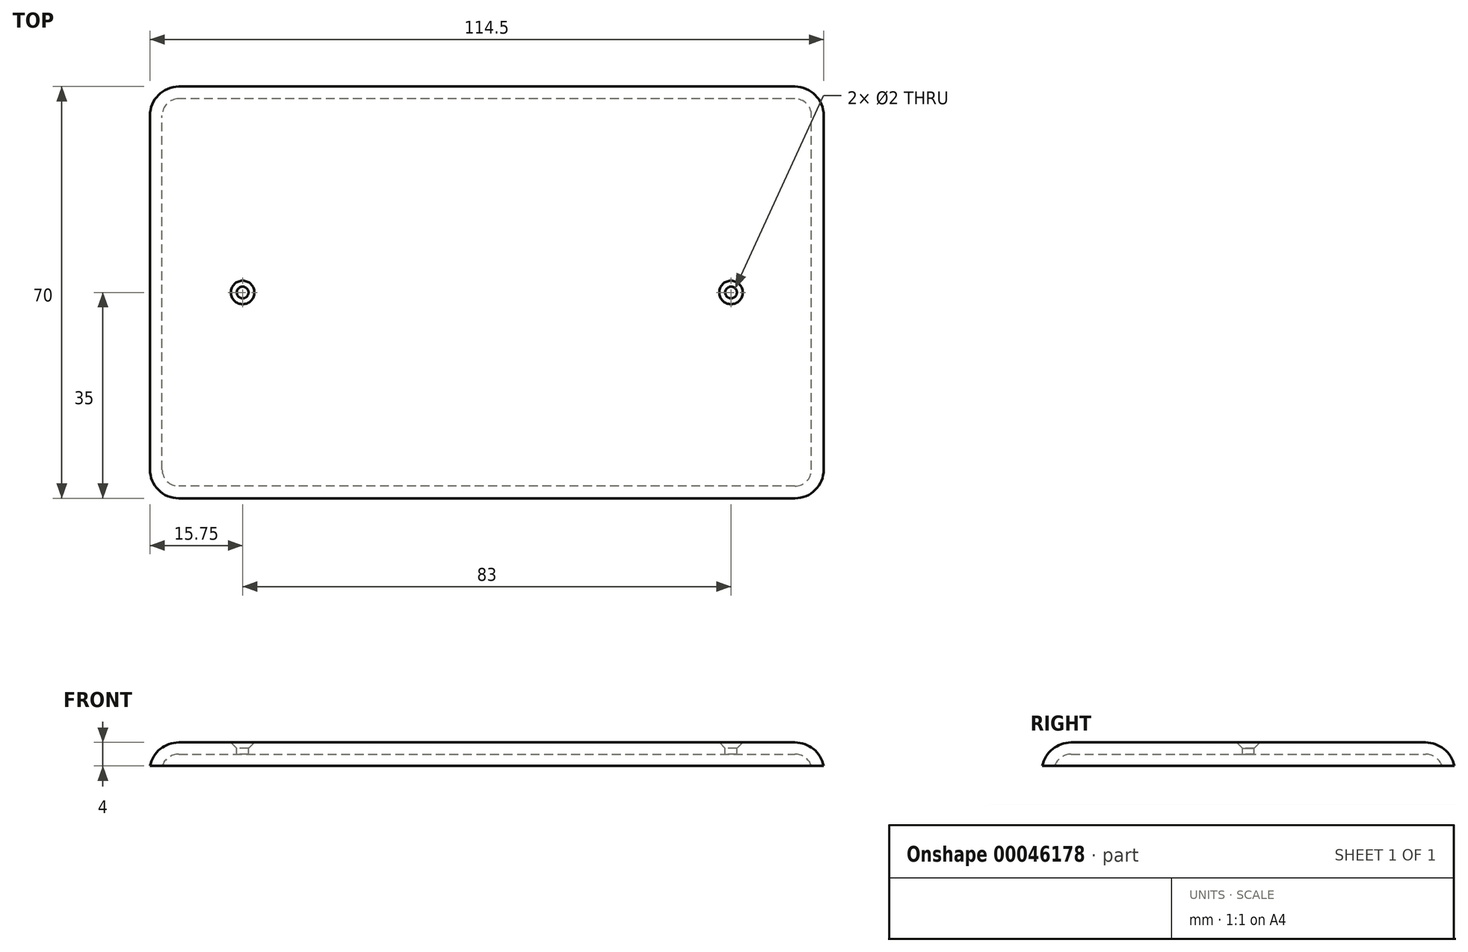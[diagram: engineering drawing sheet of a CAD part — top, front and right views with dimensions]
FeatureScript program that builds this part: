
annotation { "Feature Type Name" : "Feature", "Feature Type Description" : "" }
export const myFeature = defineFeature(function(context is Context, id is Id, definition is map)
    precondition{}
    {
        {
            var Q0;
            Q0=qCreatedBy(makeId("Top.planeOp"),FACE);
            var sketch = newSketch(context, id + "F0", { "sketchPlane" : qUnion([Q0])});
            skLineSegment(sketch, "E0.bottom", {"start": v(57.25, -35) * mm, "end": v(-57.25, -35) * mm});
            skLineSegment(sketch, "E0.top", {"start": v(57.25, 35) * mm, "end": v(-57.25, 35) * mm});
            skLineSegment(sketch, "E0.left", {"start": v(57.25, -35) * mm, "end": v(57.25, 35) * mm});
            skLineSegment(sketch, "E0.right", {"start": v(-57.25, -35) * mm, "end": v(-57.25, 35) * mm});
            skPoint(sketch, "E0.middle", {"position": v(0, 0) * mm});
            skSolve(sketch);
        }
        {
            var Q0;
            Q0=makeQuery(id+"F0.imprint","IMPRINT",FACE,{"disambiguationData":[TD([[makeQuery(id+"F0.imprint","IMPRINT",EDGE,{"derivedFrom":sQuery(id+"F0.wireOp",EDGE,"E0.bottom")}),-1.0]])]});
            extrude(context, id + "F1", {"entities" : qUnion([Q0]), "depth" : 4 * mm});
        }
        {
            var Q0;
            Q0=makeQuery(id+"F1.opExtrude","CAP_EDGE",EDGE,{"disambiguationData":[OSD([sQuery(id+"F0.wireOp",EDGE,"E0.bottom")])],"isStart":false});
            var Q1;
            Q1=makeQuery(id+"F1.opExtrude","CAP_EDGE",EDGE,{"disambiguationData":[OSD([sQuery(id+"F0.wireOp",EDGE,"E0.left")])],"isStart":false});
            var Q2;
            Q2=makeQuery(id+"F1.opExtrude","CAP_EDGE",EDGE,{"disambiguationData":[OSD([sQuery(id+"F0.wireOp",EDGE,"E0.top")])],"isStart":false});
            var Q3;
            Q3=makeQuery(id+"F1.opExtrude","CAP_EDGE",EDGE,{"disambiguationData":[OSD([sQuery(id+"F0.wireOp",EDGE,"E0.right")])],"isStart":false});
            fillet(context, id + "F2", {"entities" : qUnion([Q0, Q1, Q2, Q3]), "radius" : 5 * mm, "tangentPropagation" : true, "allowEdgeOverflow" : false});
        }
        {
            var Q0;
            Q0=makeQuery(id+"F2.opFillet","BLEND_EDGE",EDGE,{"blendedFrom":[makeQuery(id+"F1.opExtrude","CAP_EDGE",EDGE,{"disambiguationData":[OSD([sQuery(id+"F0.wireOp",EDGE,"E0.bottom")])],"isStart":false}),makeQuery(id+"F1.opExtrude","CAP_EDGE",EDGE,{"disambiguationData":[OSD([sQuery(id+"F0.wireOp",EDGE,"E0.left")])],"isStart":false})],"blendedInto":[]});
            var Q1;
            Q1=makeQuery(id+"F2.opFillet","BLEND_EDGE",EDGE,{"blendedFrom":[makeQuery(id+"F1.opExtrude","CAP_EDGE",EDGE,{"disambiguationData":[OSD([sQuery(id+"F0.wireOp",EDGE,"E0.top")])],"isStart":false}),makeQuery(id+"F1.opExtrude","CAP_EDGE",EDGE,{"disambiguationData":[OSD([sQuery(id+"F0.wireOp",EDGE,"E0.left")])],"isStart":false})],"blendedInto":[]});
            var Q2;
            Q2=makeQuery(id+"F2.opFillet","BLEND_EDGE",EDGE,{"blendedFrom":[makeQuery(id+"F1.opExtrude","CAP_EDGE",EDGE,{"disambiguationData":[OSD([sQuery(id+"F0.wireOp",EDGE,"E0.bottom")])],"isStart":false}),makeQuery(id+"F1.opExtrude","CAP_EDGE",EDGE,{"disambiguationData":[OSD([sQuery(id+"F0.wireOp",EDGE,"E0.right")])],"isStart":false})],"blendedInto":[]});
            var Q3;
            Q3=makeQuery(id+"F2.opFillet","BLEND_EDGE",EDGE,{"blendedFrom":[makeQuery(id+"F1.opExtrude","CAP_EDGE",EDGE,{"disambiguationData":[OSD([sQuery(id+"F0.wireOp",EDGE,"E0.top")])],"isStart":false}),makeQuery(id+"F1.opExtrude","CAP_EDGE",EDGE,{"disambiguationData":[OSD([sQuery(id+"F0.wireOp",EDGE,"E0.right")])],"isStart":false})],"blendedInto":[]});
            fillet(context, id + "F3", {"entities" : qUnion([Q0, Q1, Q2, Q3]), "radius" : 5 * mm, "tangentPropagation" : true, "allowEdgeOverflow" : false});
        }
        {
            var Q0;
            Q0=makeQuery(id+"F1.opExtrude","CAP_FACE",FACE,{"disambiguationData":[OSD([sQuery(id+"F0.wireOp",EDGE,"E0.bottom"),sQuery(id+"F0.wireOp",EDGE,"E0.top"),sQuery(id+"F0.wireOp",EDGE,"E0.left"),sQuery(id+"F0.wireOp",EDGE,"E0.right")])],"isStart":true});
            shell(context, id + "F4", {"entities" : qUnion([Q0]), "thickness" : 2 * mm});
        }
        {
            var Q0;
            Q0=makeQuery(id+"F1.opExtrude","CAP_FACE",FACE,{"disambiguationData":[OSD([sQuery(id+"F0.wireOp",EDGE,"E0.bottom"),sQuery(id+"F0.wireOp",EDGE,"E0.top"),sQuery(id+"F0.wireOp",EDGE,"E0.left"),sQuery(id+"F0.wireOp",EDGE,"E0.right")])],"isStart":false});
            var sketch = newSketch(context, id + "F5", { "sketchPlane" : qUnion([Q0])});
            skSolve(sketch);
        }
        {
            var Q0;
            {var subQ0=sQuery(id+"F0.wireOp",EDGE,"E0.right");var subQ1=sQuery(id+"F0.wireOp",EDGE,"E0.left");var subQ2=sQuery(id+"F0.wireOp",EDGE,"E0.top");var subQ3=sQuery(id+"F0.wireOp",EDGE,"E0.bottom");var subQ4=makeQuery(id+"F1.opExtrude","CAP_FACE",FACE,{"disambiguationData":[OSD([subQ3,subQ2,subQ1,subQ0])],"isStart":false});Q0=makeQuery(id+"F5.imprint","IMPRINT",FACE,{"disambiguationData":[TD([[makeQuery(id+"F5.imprint","IMPRINT",EDGE,{"derivedFrom":makeQuery(id+"F2.opFillet","BLEND_EDGE",EDGE,{"blendedFrom":[makeQuery(id+"F1.opExtrude","CAP_EDGE",EDGE,{"disambiguationData":[OSD([subQ3])],"isStart":false}),subQ4],"blendedInto":[subQ4]})}),1.0]])]});}
            var sketch = newSketch(context, id + "F6", { "sketchPlane" : qUnion([Q0])});
            skLineSegment(sketch, "E1", {"start": v(-58.43, 0) * mm, "end": v(58.37, 0) * mm, "construction": true});
            skPoint(sketch, "E2", {"position": v(-41.5, 0) * mm});
            skPoint(sketch, "E3", {"position": v(41.5, 0) * mm});
            skSolve(sketch);
        }
        {
            var Q0;
            Q0=sQuery(id+"F6.wireOp",VERTEX,"E2");
            var Q1;
            Q1=sQuery(id+"F6.wireOp",VERTEX,"E3");
            var Q2;
            Q2=makeQuery(id+"F1.opExtrude","SWEPT_BODY",BODY,{"disambiguationData":[OSD([sQuery(id+"F0.wireOp",EDGE,"E0.bottom"),sQuery(id+"F0.wireOp",EDGE,"E0.top"),sQuery(id+"F0.wireOp",EDGE,"E0.left"),sQuery(id+"F0.wireOp",EDGE,"E0.right")])]});
            hole(context, id + "F7", {"style" : HoleStyle.C_SINK, "endStyle" : HoleEndStyle.THROUGH, "holeDiameter" : 2 * mm, "cSinkDiameter" : 4 * mm, "cSinkAngle" : 90 * degree, "locations" : qUnion([Q0, Q1]), "scope" : qUnion([Q2]), "isTappedThrough" : true});
        }
    });
